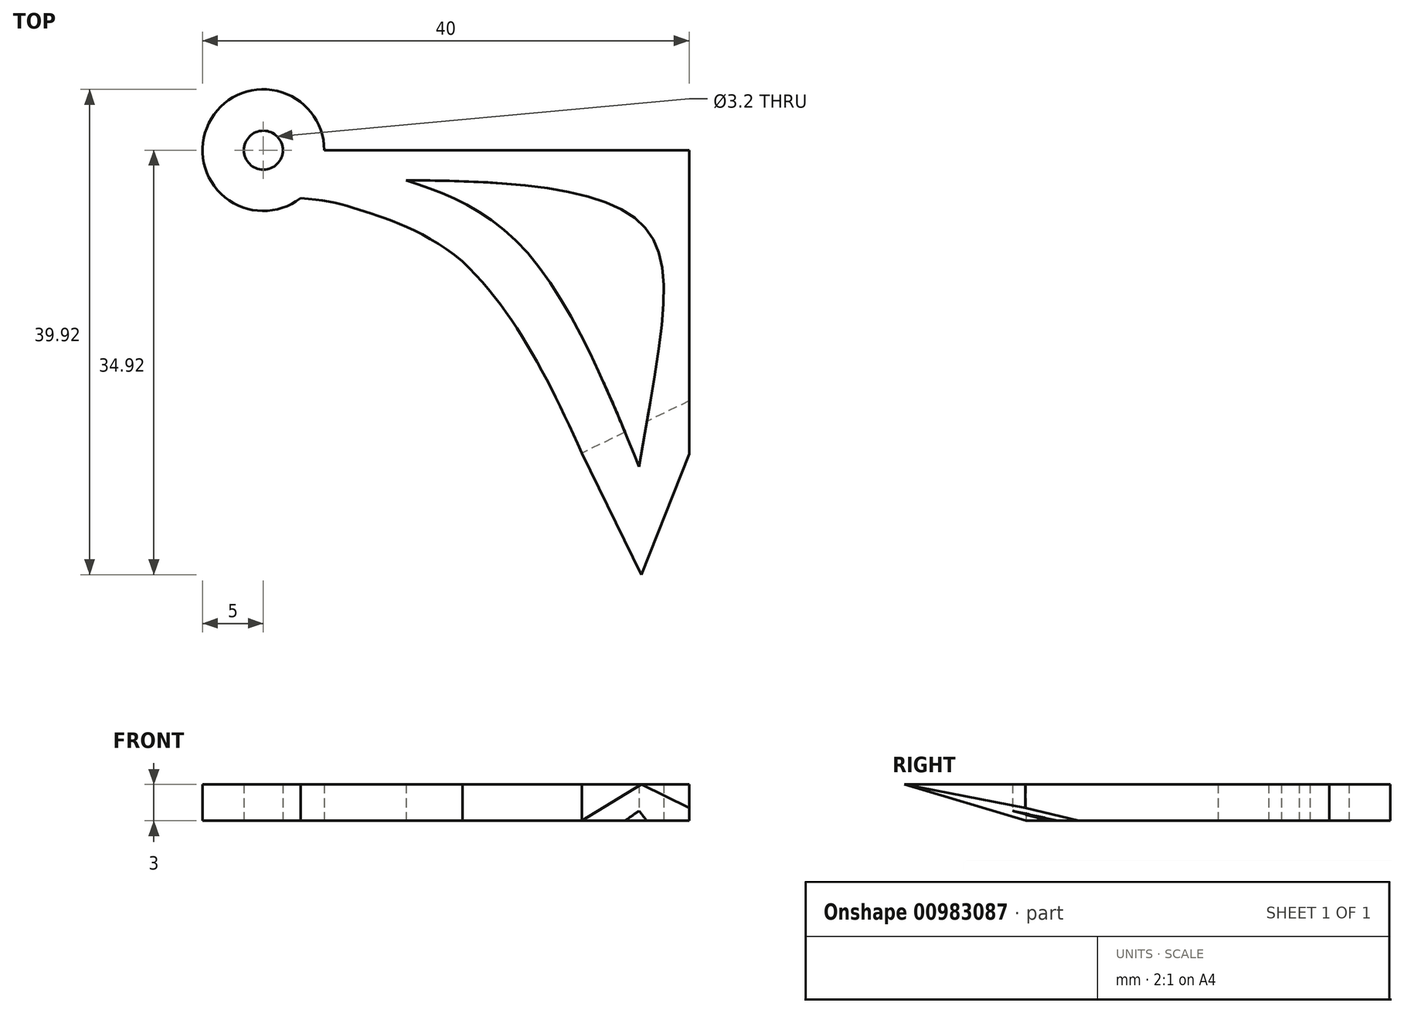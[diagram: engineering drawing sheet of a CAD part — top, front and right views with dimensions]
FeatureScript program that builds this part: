
annotation { "Feature Type Name" : "Feature", "Feature Type Description" : "" }
export const myFeature = defineFeature(function(context is Context, id is Id, definition is map)
    precondition{}
    {
        {
            var Q0;
            Q0=qCreatedBy(makeId("Top.planeOp"),FACE);
            var sketch = newSketch(context, id + "F0", { "sketchPlane" : qUnion([Q0])});
            skLineSegment(sketch, "E0", {"start": v(0, 0) * mm, "end": v(35, 0) * mm});
            skLineSegment(sketch, "E1", {"start": v(35, 0) * mm, "end": v(35, -25) * mm});
            skLineSegment(sketch, "E2", {"start": v(35, -25) * mm, "end": v(31.06, -34.92) * mm});
            skLineSegment(sketch, "E3", {"start": v(31.06, -34.92) * mm, "end": v(26.18, -24.92) * mm});
            skFitSpline(sketch, "E4", {"points": [v(0, 0) * mm, v(16.36, -9.15) * mm, v(26.18, -24.92) * mm], "startDerivative": vector(36.1, -14.86) * mm, "endDerivative": vector(16.17, -35.79) * mm});
            skCircle(sketch, "E5", {"center": v(0, 0) * mm, "radius": 5 * mm});
            skCircle(sketch, "E6", {"center": v(0, 0) * mm, "radius": 1.6 * mm});
            skFitSpline(sketch, "E7", {"points": [v(3.05, -3.96) * mm, v(8.4, -5.06) * mm, v(16.36, -9.15) * mm], "startDerivative": vector(15.34, -0.75) * mm, "endDerivative": vector(15.34, -12.8) * mm});
            skFitSpline(sketch, "E8", {"points": [v(30.89, -26.03) * mm, v(21.69, -8.42) * mm, v(11.75, -2.48) * mm], "startDerivative": vector(-9.33, 22.47) * mm, "endDerivative": vector(-21.56, 7.09) * mm});
            skFitSpline(sketch, "E9", {"points": [v(30.89, -26.03) * mm, v(30.89, -5.87) * mm, v(11.75, -2.48) * mm], "startDerivative": vector(10.79, 65.6) * mm, "endDerivative": vector(-44.6, 0.34) * mm});
            skSolve(sketch);
        }
        {
            var Q0;
            {var subQ1=sQuery(id+"F0.wireOp",EDGE,"E1");Q0=makeQuery(id+"F0.imprint","IMPRINT",FACE,{"disambiguationData":[TD([[makeQuery(id+"F0.imprint","IMPRINT",EDGE,{"derivedFrom":subQ1}),-1.0]])]});}
            var Q1;
            {var subQ0=sQuery(id+"F0.wireOp",EDGE,"E5");var subQ1=sQuery(id+"F0.wireOp",EDGE,"E0");var subQ2=makeQuery(id+"F0.imprint","INTERSECT",VERTEX,{"derivedFrom":[subQ1,subQ0]});Q1=makeQuery(id+"F0.imprint","IMPRINT",FACE,{"disambiguationData":[TD([[makeQuery(id+"F0.imprint","IMPRINT",EDGE,{"disambiguationData":[TD([[subQ2,1.0]])],"derivedFrom":subQ1}),1.0]])]});}
            var Q2;
            {var subQ0=sQuery(id+"F0.wireOp",EDGE,"E5");var subQ1=sQuery(id+"F0.wireOp",EDGE,"E0");var subQ2=makeQuery(id+"F0.imprint","INTERSECT",VERTEX,{"derivedFrom":[subQ1,subQ0]});Q2=makeQuery(id+"F0.imprint","IMPRINT",FACE,{"disambiguationData":[TD([[makeQuery(id+"F0.imprint","IMPRINT",EDGE,{"disambiguationData":[TD([[subQ2,1.0]])],"derivedFrom":subQ1}),-1.0]])]});}
            var Q3;
            {var subQ0=sQuery(id+"F0.wireOp",EDGE,"E7");Q3=makeQuery(id+"F0.imprint","IMPRINT",FACE,{"disambiguationData":[TD([[makeQuery(id+"F0.imprint","IMPRINT",EDGE,{"derivedFrom":subQ0}),1.0]])]});}
            extrude(context, id + "F1", {"entities" : qUnion([Q0, Q1, Q2, Q3]), "depth" : 3 * mm, "offsetDistance" : 25 * mm});
        }
        {
            var Q0;
            Q0=makeQuery(id+"F1.opExtrude","SWEPT_FACE",FACE,{"disambiguationData":[OSD([sQuery(id+"F0.wireOp",EDGE,"E3")])]});
            var sketch = newSketch(context, id + "F2", { "sketchPlane" : qUnion([Q0])});
            skLineSegment(sketch, "E10", {"start": v(45.01, 3) * mm, "end": v(33.88, 0) * mm});
            skSolve(sketch);
        }
        {
            var Q0;
            Q0=makeQuery(id+"F2.imprint","IMPRINT",FACE,{"disambiguationData":[TD([[makeQuery(id+"F2.imprint","IMPRINT",EDGE,{"derivedFrom":sQuery(id+"F2.wireOp",EDGE,"E10")}),1.0]])]});
            extrude(context, id + "F3", {"entities" : qUnion([Q0]), "operationType" : NewBodyOperationType.REMOVE, "oppositeDirection" : true, "depth" : 10 * mm, "offsetDistance" : 25 * mm});
        }
    });
